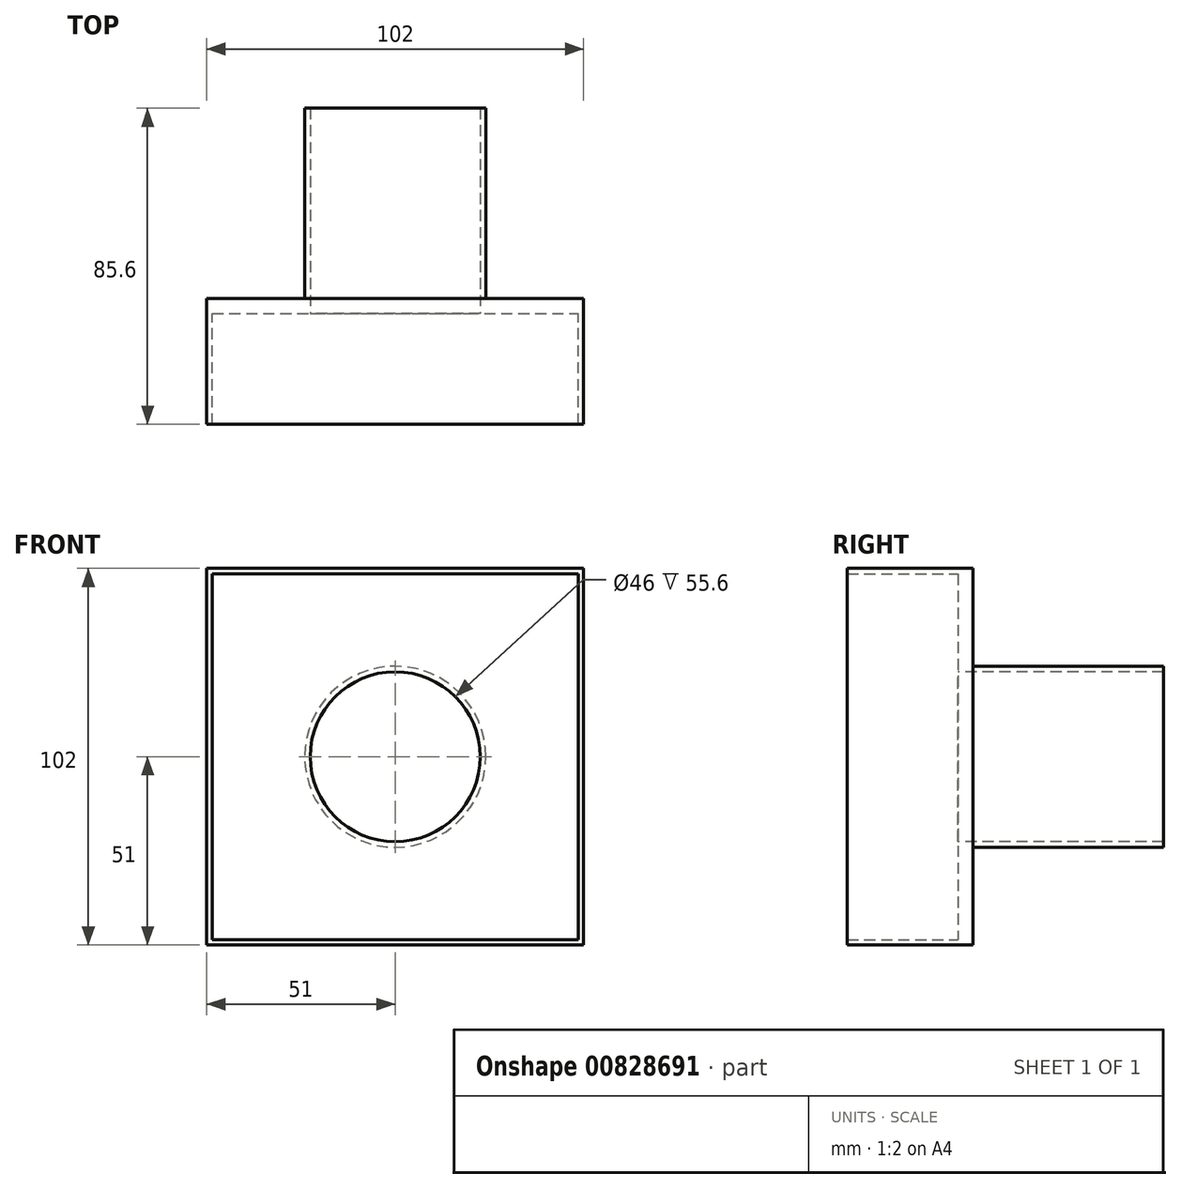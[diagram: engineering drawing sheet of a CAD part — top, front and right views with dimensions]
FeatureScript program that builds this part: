
annotation { "Feature Type Name" : "Feature", "Feature Type Description" : "" }
export const myFeature = defineFeature(function(context is Context, id is Id, definition is map)
    precondition{}
    {
        {
            var Q0;
            Q0=qCreatedBy(makeId("Front.planeOp"),FACE);
            var sketch = newSketch(context, id + "F0", { "sketchPlane" : qUnion([Q0])});
            skLineSegment(sketch, "E0.bottom", {"start": v(48, -48) * mm, "end": v(-48, -48) * mm});
            skLineSegment(sketch, "E0.top", {"start": v(48, 48) * mm, "end": v(-48, 48) * mm});
            skLineSegment(sketch, "E0.left", {"start": v(48, -48) * mm, "end": v(48, 48) * mm});
            skLineSegment(sketch, "E0.right", {"start": v(-48, -48) * mm, "end": v(-48, 48) * mm});
            skPoint(sketch, "E0.middle", {"position": v(0, 0) * mm});
            skLineSegment(sketch, "E1.0", {"start": v(51, 51) * mm, "end": v(-51, 51) * mm});
            skLineSegment(sketch, "E1.1", {"start": v(51, -51) * mm, "end": v(51, 51) * mm});
            skLineSegment(sketch, "E1.2", {"start": v(51, -51) * mm, "end": v(-51, -51) * mm});
            skLineSegment(sketch, "E1.3", {"start": v(-51, -51) * mm, "end": v(-51, 51) * mm});
            skSolve(sketch);
        }
        {
            var Q0;
            Q0=makeQuery(id+"F0.imprint","IMPRINT",FACE,{"disambiguationData":[TD([[makeQuery(id+"F0.imprint","IMPRINT",EDGE,{"derivedFrom":sQuery(id+"F0.wireOp",EDGE,"E0.bottom")}),1.0]])]});
            var Q1;
            Q1=makeQuery(id+"F0.imprint","IMPRINT",FACE,{"disambiguationData":[TD([[makeQuery(id+"F0.imprint","IMPRINT",EDGE,{"derivedFrom":sQuery(id+"F0.wireOp",EDGE,"E0.bottom")}),-1.0]])]});
            extrude(context, id + "F1", {"entities" : qUnion([Q0, Q1]), "depth" : 4 * mm, "offsetDistance" : 25 * mm});
        }
        {
            var Q0;
            Q0=makeQuery(id+"F1.opExtrude","CAP_FACE",FACE,{"disambiguationData":[OSD([sQuery(id+"F0.wireOp",EDGE,"E1.0"),sQuery(id+"F0.wireOp",EDGE,"E1.1"),sQuery(id+"F0.wireOp",EDGE,"E1.2"),sQuery(id+"F0.wireOp",EDGE,"E1.3")])],"isStart":false});
            var sketch = newSketch(context, id + "F2", { "sketchPlane" : qUnion([Q0])});
            skLineSegment(sketch, "E2.bottom", {"start": v(49.5, -49.5) * mm, "end": v(-49.5, -49.5) * mm});
            skLineSegment(sketch, "E2.top", {"start": v(49.5, 49.5) * mm, "end": v(-49.5, 49.5) * mm});
            skLineSegment(sketch, "E2.left", {"start": v(49.5, -49.5) * mm, "end": v(49.5, 49.5) * mm});
            skLineSegment(sketch, "E2.right", {"start": v(-49.5, -49.5) * mm, "end": v(-49.5, 49.5) * mm});
            skPoint(sketch, "E2.middle", {"position": v(0, 0) * mm});
            skLineSegment(sketch, "E3.bottom", {"start": v(48, -48) * mm, "end": v(-48, -48) * mm});
            skLineSegment(sketch, "E3.top", {"start": v(48, 48) * mm, "end": v(-48, 48) * mm});
            skLineSegment(sketch, "E3.left", {"start": v(48, -48) * mm, "end": v(48, 48) * mm});
            skLineSegment(sketch, "E3.right", {"start": v(-48, -48) * mm, "end": v(-48, 48) * mm});
            skSolve(sketch);
        }
        {
            var Q0;
            Q0=makeQuery(id+"F2.imprint","IMPRINT",FACE,{"disambiguationData":[TD([[makeQuery(id+"F2.imprint","IMPRINT",EDGE,{"derivedFrom":sQuery(id+"F2.wireOp",EDGE,"E2.bottom")}),1.0]])]});
            extrude(context, id + "F3", {"entities" : qUnion([Q0]), "operationType" : NewBodyOperationType.ADD, "depth" : 30 * mm, "offsetDistance" : 25 * mm, "hasSecondDirection" : true, "secondDirectionOppositeDirection" : true, "secondDirectionDepth" : 4 * mm});
        }
        {
            var Q0;
            Q0=makeQuery(id+"F1.opExtrude","CAP_FACE",FACE,{"disambiguationData":[OSD([sQuery(id+"F0.wireOp",EDGE,"E1.0"),sQuery(id+"F0.wireOp",EDGE,"E1.1"),sQuery(id+"F0.wireOp",EDGE,"E1.2"),sQuery(id+"F0.wireOp",EDGE,"E1.3")])],"isStart":false});
            var sketch = newSketch(context, id + "F4", { "sketchPlane" : qUnion([Q0])});
            skCircle(sketch, "E4", {"center": v(0, 0) * mm, "radius": 24.5 * mm});
            skCircle(sketch, "E5", {"center": v(0, 0) * mm, "radius": 23 * mm});
            skSolve(sketch);
        }
        {
            var Q0;
            Q0=makeQuery(id+"F4.imprint","IMPRINT",FACE,{"disambiguationData":[TD([[makeQuery(id+"F4.imprint","IMPRINT",EDGE,{"derivedFrom":sQuery(id+"F4.wireOp",EDGE,"E5")}),1.0]])]});
            extrude(context, id + "F5", {"entities" : qUnion([Q0]), "operationType" : NewBodyOperationType.REMOVE, "oppositeDirection" : true, "depth" : 25 * mm, "offsetDistance" : 25 * mm});
        }
        {
            var Q0;
            Q0=makeQuery(id+"F1.opExtrude","CAP_FACE",FACE,{"disambiguationData":[OSD([sQuery(id+"F0.wireOp",EDGE,"E1.0"),sQuery(id+"F0.wireOp",EDGE,"E1.1"),sQuery(id+"F0.wireOp",EDGE,"E1.2"),sQuery(id+"F0.wireOp",EDGE,"E1.3")])],"isStart":false});
            var sketch = newSketch(context, id + "F6", { "sketchPlane" : qUnion([Q0])});
            skCircle(sketch, "E6", {"center": v(0, 0) * mm, "radius": 24.5 * mm});
            skSolve(sketch);
        }
        {
            var Q0;
            Q0=makeQuery(id+"F6.imprint","IMPRINT",FACE,{"disambiguationData":[TD([[makeQuery(id+"F6.imprint","IMPRINT",EDGE,{"derivedFrom":sQuery(id+"F6.wireOp",EDGE,"E6")}),1.0]])]});
            extrude(context, id + "F7", {"entities" : qUnion([Q0]), "operationType" : NewBodyOperationType.ADD, "oppositeDirection" : true, "depth" : 55.6 * mm, "offsetDistance" : 25 * mm});
        }
    });
